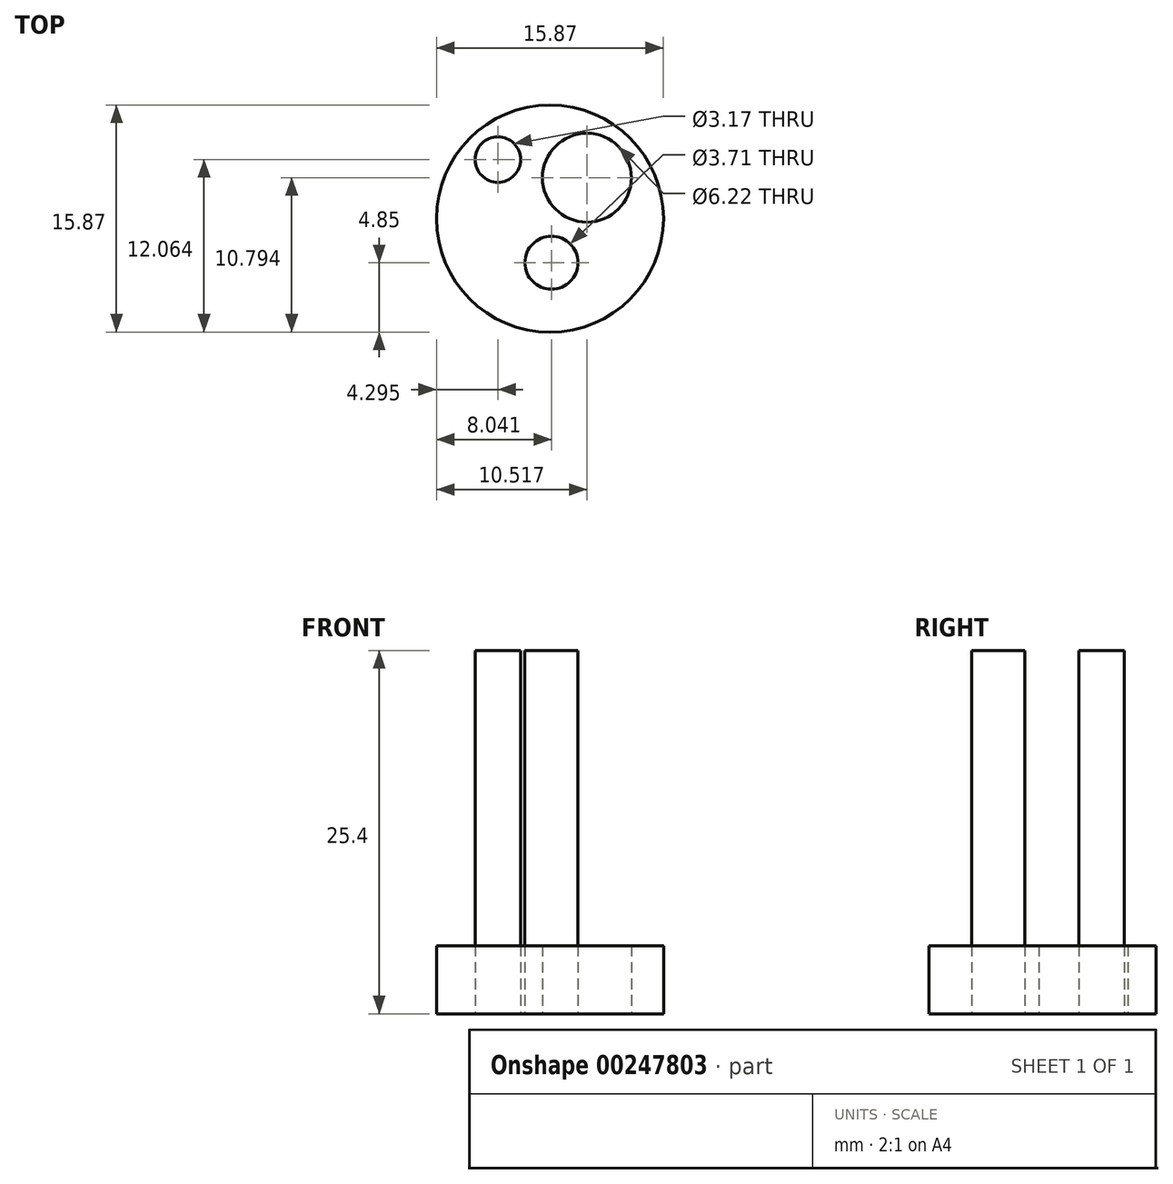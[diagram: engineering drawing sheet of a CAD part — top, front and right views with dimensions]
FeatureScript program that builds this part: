
annotation { "Feature Type Name" : "Feature", "Feature Type Description" : "" }
export const myFeature = defineFeature(function(context is Context, id is Id, definition is map)
    precondition{}
    {
        {
            var Q0;
            Q0=qCreatedBy(makeId("Top.planeOp"),FACE);
            var sketch = newSketch(context, id + "F0", { "sketchPlane" : qUnion([Q0])});
            skCircle(sketch, "E0", {"center": v(0.94, -1.11) * mm, "radius": 3.33 * mm, "construction": true});
            skCircle(sketch, "E1", {"center": v(0.94, -1.11) * mm, "radius": 1.85 * mm, "construction": true});
            skCircle(sketch, "E2", {"center": v(-2.8, 6.1) * mm, "radius": 1.59 * mm, "construction": true});
            skCircle(sketch, "E3", {"center": v(3.42, 4.83) * mm, "radius": 2.86 * mm, "construction": true});
            skCircle(sketch, "E4", {"center": v(3.42, 4.83) * mm, "radius": 1.27 * mm, "construction": true});
            skCircle(sketch, "E5", {"center": v(-1.54, -7.05) * mm, "radius": 2.86 * mm, "construction": true});
            skCircle(sketch, "E6", {"center": v(-1.54, -7.05) * mm, "radius": 1.27 * mm, "construction": true});
            skLineSegment(sketch, "E7", {"start": v(-1.54, -7.05) * mm, "end": v(3.42, 4.83) * mm, "construction": true});
            skCircle(sketch, "E8", {"center": v(0.94, -1.11) * mm, "radius": 4.85 * mm, "construction": true});
            skLineSegment(sketch, "E9", {"start": v(-4.4, 6.1) * mm, "end": v(-4.4, -7.05) * mm, "construction": true});
            skLineSegment(sketch, "E10", {"start": v(-2.8, 7.7) * mm, "end": v(3.42, 7.7) * mm, "construction": true});
            skLineSegment(sketch, "E11", {"start": v(-6.93, 10.23) * mm, "end": v(15.8, 10.23) * mm, "construction": true});
            skLineSegment(sketch, "E12", {"start": v(-6.93, -12.45) * mm, "end": v(16.66, -12.45) * mm, "construction": true});
            skLineSegment(sketch, "E13", {"start": v(-6.93, 10.23) * mm, "end": v(-6.93, -12.45) * mm, "construction": true});
            skLineSegment(sketch, "E14", {"start": v(-6.93, -1.11) * mm, "end": v(0.94, -1.11) * mm, "construction": true});
            skSolve(sketch);
        }
        {
            var Q0;
            Q0=qCreatedBy(makeId("Top.planeOp"),FACE);
            var sketch = newSketch(context, id + "F1", { "sketchPlane" : qUnion([Q0])});
            skCircle(sketch, "E15", {"center": v(3.42, 4.83) * mm, "radius": 3.11 * mm});
            skCircle(sketch, "E16", {"center": v(0.94, -1.11) * mm, "radius": 1.85 * mm});
            skCircle(sketch, "E17", {"center": v(-2.8, 6.1) * mm, "radius": 1.59 * mm});
            skCircle(sketch, "E18", {"center": v(0.79, 3.23) * mm, "radius": 6.2 * mm, "construction": true});
            skCircle(sketch, "E19", {"center": v(0.83, 1.97) * mm, "radius": 7.94 * mm});
            skLineSegment(sketch, "E20", {"start": v(0.79, 3.23) * mm, "end": v(0.94, -1.11) * mm, "construction": true});
            skSolve(sketch);
        }
        {
            var Q0;
            Q0 = qSketchRegion(id + "F1", true);
            extrude(context, id + "F2", {"entities" : qUnion([Q0]), "depth" : 4.76 * mm});
        }
        {
            var Q0;
            Q0=makeQuery(id+"F2.opExtrude","CAP_FACE",FACE,{"disambiguationData":[OSD([sQuery(id+"F1.wireOp",EDGE,"E15"),sQuery(id+"F1.wireOp",EDGE,"E16"),sQuery(id+"F1.wireOp",EDGE,"E17"),sQuery(id+"F1.wireOp",EDGE,"SCur8SKD-ehf7-vBM6-Sg3h-crRM3vHgMNT9.bottom"),sQuery(id+"F1.wireOp",EDGE,"SCur8SKD-ehf7-vBM6-Sg3h-crRM3vHgMNT9.top"),sQuery(id+"F1.wireOp",EDGE,"SCur8SKD-ehf7-vBM6-Sg3h-crRM3vHgMNT9.left"),sQuery(id+"F1.wireOp",EDGE,"SCur8SKD-ehf7-vBM6-Sg3h-crRM3vHgMNT9.right")])],"isStart":true});
            var sketch = newSketch(context, id + "F3", { "sketchPlane" : qUnion([Q0])});
            skCircle(sketch, "E21.0", {"center": v(0.94, 1.11) * mm, "radius": 1.85 * mm, "construction": true});
            skCircle(sketch, "E21.1", {"center": v(-2.8, -6.1) * mm, "radius": 1.59 * mm, "construction": true});
            skSolve(sketch);
        }
        {
            var Q0;
            Q0=makeQuery(id+"F3.imprint","IMPRINT",FACE,{"disambiguationData":[TD([[makeQuery(id+"F3.imprint","IMPRINT",EDGE,{"derivedFrom":makeQuery(id+"F2.opExtrude","CAP_EDGE",EDGE,{"disambiguationData":[OSD([sQuery(id+"F1.wireOp",EDGE,"E17")])],"isStart":true})}),-1.0]])]});
            var Q1;
            Q1=makeQuery(id+"F3.imprint","IMPRINT",FACE,{"disambiguationData":[TD([[makeQuery(id+"F3.imprint","IMPRINT",EDGE,{"derivedFrom":makeQuery(id+"F2.opExtrude","CAP_EDGE",EDGE,{"disambiguationData":[OSD([sQuery(id+"F1.wireOp",EDGE,"E16")])],"isStart":true})}),-1.0]])]});
            extrude(context, id + "F4", {"entities" : qUnion([Q0, Q1]), "oppositeDirection" : true, "depth" : 25.4 * mm});
        }
    });
